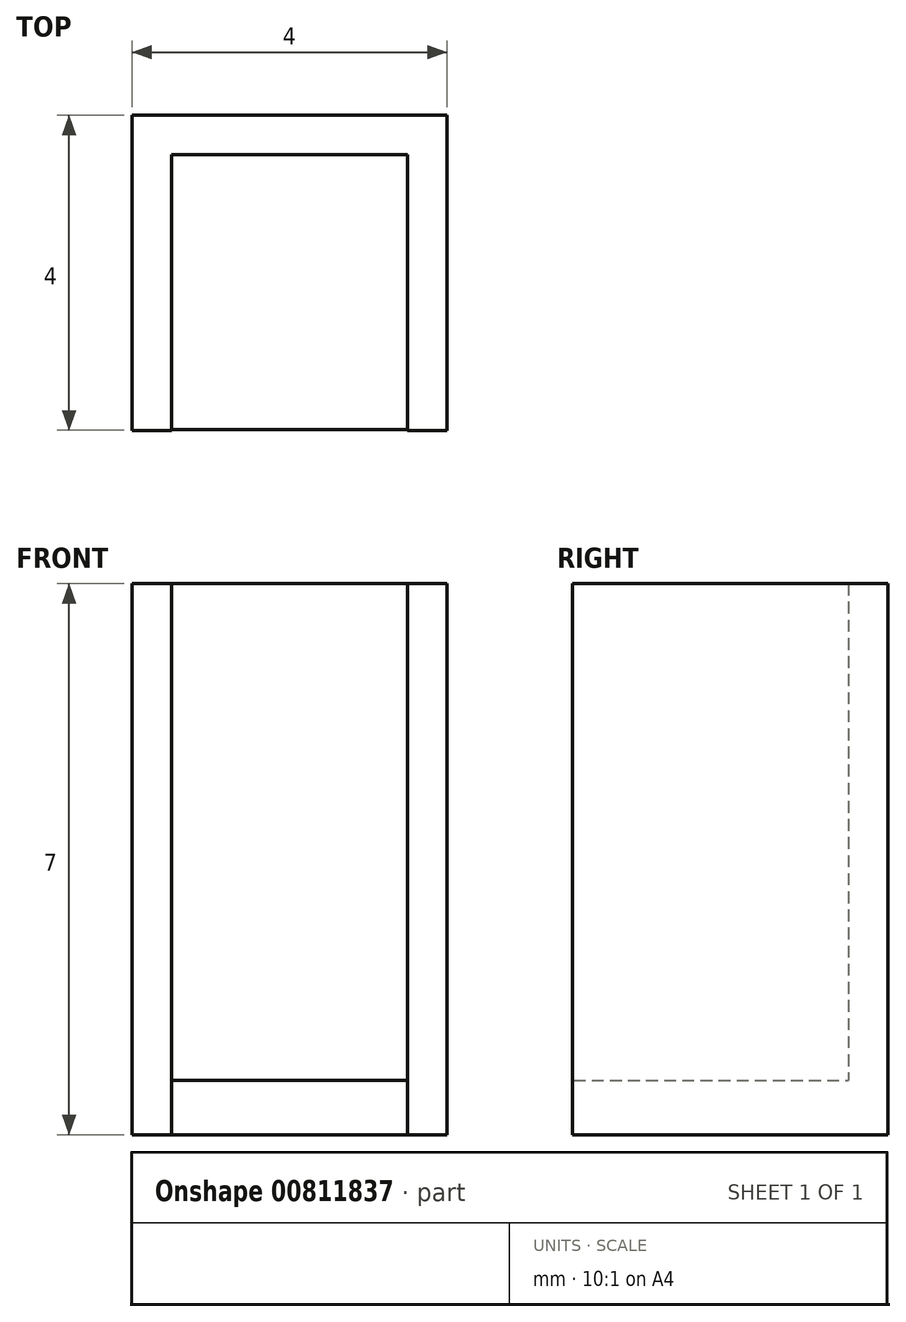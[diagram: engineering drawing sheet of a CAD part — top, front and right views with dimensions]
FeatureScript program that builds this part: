
annotation { "Feature Type Name" : "Feature", "Feature Type Description" : "" }
export const myFeature = defineFeature(function(context is Context, id is Id, definition is map)
    precondition{}
    {
        {
            var Q0;
            Q0=qCreatedBy(makeId("Top.planeOp"),FACE);
            var sketch = newSketch(context, id + "F0", { "sketchPlane" : qUnion([Q0])});
            skArc(sketch, "E0", {"start": v(-11, -10.87) * mm, "mid": v(0, -16.37) * mm, "end": v(11, -10.87) * mm});
            skLineSegment(sketch, "E1.right", {"start": v(-11, 5.63) * mm, "end": v(-11, -10.87) * mm});
            skLineSegment(sketch, "E2.right", {"start": v(11, 5.63) * mm, "end": v(11, -10.87) * mm});
            skArc(sketch, "E3.trimOffspring", {"start": v(11, 5.63) * mm, "mid": v(0, 11.13) * mm, "end": v(-11, 5.63) * mm});
            skArc(sketch, "E4", {"start": v(-2, 2.86) * mm, "mid": v(0, -13.9) * mm, "end": v(2, 2.86) * mm});
            skLineSegment(sketch, "E5.top", {"start": v(2, 6.86) * mm, "end": v(-2, 6.86) * mm});
            skLineSegment(sketch, "E5.right", {"start": v(-2, 2.86) * mm, "end": v(-2, 6.86) * mm});
            skLineSegment(sketch, "E6", {"start": v(2, 6.86) * mm, "end": v(2, 2.86) * mm});
            skSolve(sketch);
        }
        {
            var Q0;
            Q0=makeQuery(id+"F0.imprint","IMPRINT",FACE,{"disambiguationData":[TD([[makeQuery(id+"F0.imprint","IMPRINT",EDGE,{"derivedFrom":sQuery(id+"F0.wireOp",EDGE,"E0")}),1.0]])]});
            var sketch = newSketch(context, id + "F1", { "sketchPlane" : qUnion([Q0])});
            skLineSegment(sketch, "E7.bottom", {"start": v(-2, 6.86) * mm, "end": v(2, 6.86) * mm});
            skLineSegment(sketch, "E7.top", {"start": v(-2, 2.86) * mm, "end": v(-1.5, 2.86) * mm});
            skLineSegment(sketch, "E7.left", {"start": v(-2, 6.86) * mm, "end": v(-2, 2.86) * mm});
            skLineSegment(sketch, "E7.right", {"start": v(2, 6.86) * mm, "end": v(2, 2.86) * mm});
            skLineSegment(sketch, "E8.top", {"start": v(-2, 6.86) * mm, "end": v(-1.5, 6.86) * mm});
            skLineSegment(sketch, "E8.left", {"start": v(-2, 2.86) * mm, "end": v(-2, 6.86) * mm});
            skLineSegment(sketch, "E8.right", {"start": v(-1.5, 2.86) * mm, "end": v(-1.5, 6.36) * mm});
            skLineSegment(sketch, "E9.bottom", {"start": v(-1.5, 6.86) * mm, "end": v(2, 6.86) * mm});
            skLineSegment(sketch, "E9.top", {"start": v(-1.5, 6.36) * mm, "end": v(1.5, 6.36) * mm});
            skLineSegment(sketch, "E9.right", {"start": v(2, 6.86) * mm, "end": v(2, 6.36) * mm});
            skLineSegment(sketch, "E10.bottom", {"start": v(2, 6.86) * mm, "end": v(1.5, 6.86) * mm});
            skLineSegment(sketch, "E10.top", {"start": v(2, 2.86) * mm, "end": v(1.5, 2.86) * mm});
            skLineSegment(sketch, "E10.right", {"start": v(1.5, 6.36) * mm, "end": v(1.5, 2.86) * mm});
            skLineSegment(sketch, "E11.trimOffspring", {"start": v(1.5, 2.86) * mm, "end": v(2, 2.86) * mm});
            skSolve(sketch);
        }
        {
            var Q0;
            Q0 = qSketchRegion(id + "F1", true);
            var Q1;
            {var subQ5=sQuery(id+"F1.wireOp",EDGE,"E7.top");Q1=makeQuery(id+"F1.imprint","IMPRINT",FACE,{"disambiguationData":[TD([[makeQuery(id+"F1.imprint","IMPRINT",EDGE,{"derivedFrom":subQ5}),1.0]])]});}
            extrude(context, id + "F2", {"entities" : qUnion([Q0, Q1]), "depth" : 7 * mm, "offsetDistance" : 25 * mm});
        }
        {
            var Q0;
            Q0=qCreatedBy(makeId("Front.planeOp"),FACE);
            cPlane(context, id + "F3", {"entities" : qUnion([Q0]), "cplaneType" : CPlaneType.OFFSET, "offset" : 6.5 * mm, "oppositeDirection" : true, "width" : 150 * mm, "height" : 150 * mm});
        }
        {
            var Q0;
            Q0=qCreatedBy(id+"F3.planeOp",FACE);
            var sketch = newSketch(context, id + "F4", { "sketchPlane" : qUnion([Q0])});
            skLineSegment(sketch, "E12.bottom", {"start": v(-1.5, 0) * mm, "end": v(1.5, 0) * mm});
            skLineSegment(sketch, "E12.top", {"start": v(-1.5, 0.69) * mm, "end": v(1.5, 0.69) * mm});
            skLineSegment(sketch, "E12.left", {"start": v(-1.5, 0) * mm, "end": v(-1.5, 0.69) * mm});
            skLineSegment(sketch, "E12.right", {"start": v(1.5, 0) * mm, "end": v(1.5, 0.69) * mm});
            skSolve(sketch);
        }
        {
            var Q0;
            Q0 = qSketchRegion(id + "F4", true);
            extrude(context, id + "F5", {"entities" : qUnion([Q0]), "operationType" : NewBodyOperationType.ADD, "depth" : 3.63 * mm, "offsetDistance" : 25 * mm});
        }
    });
